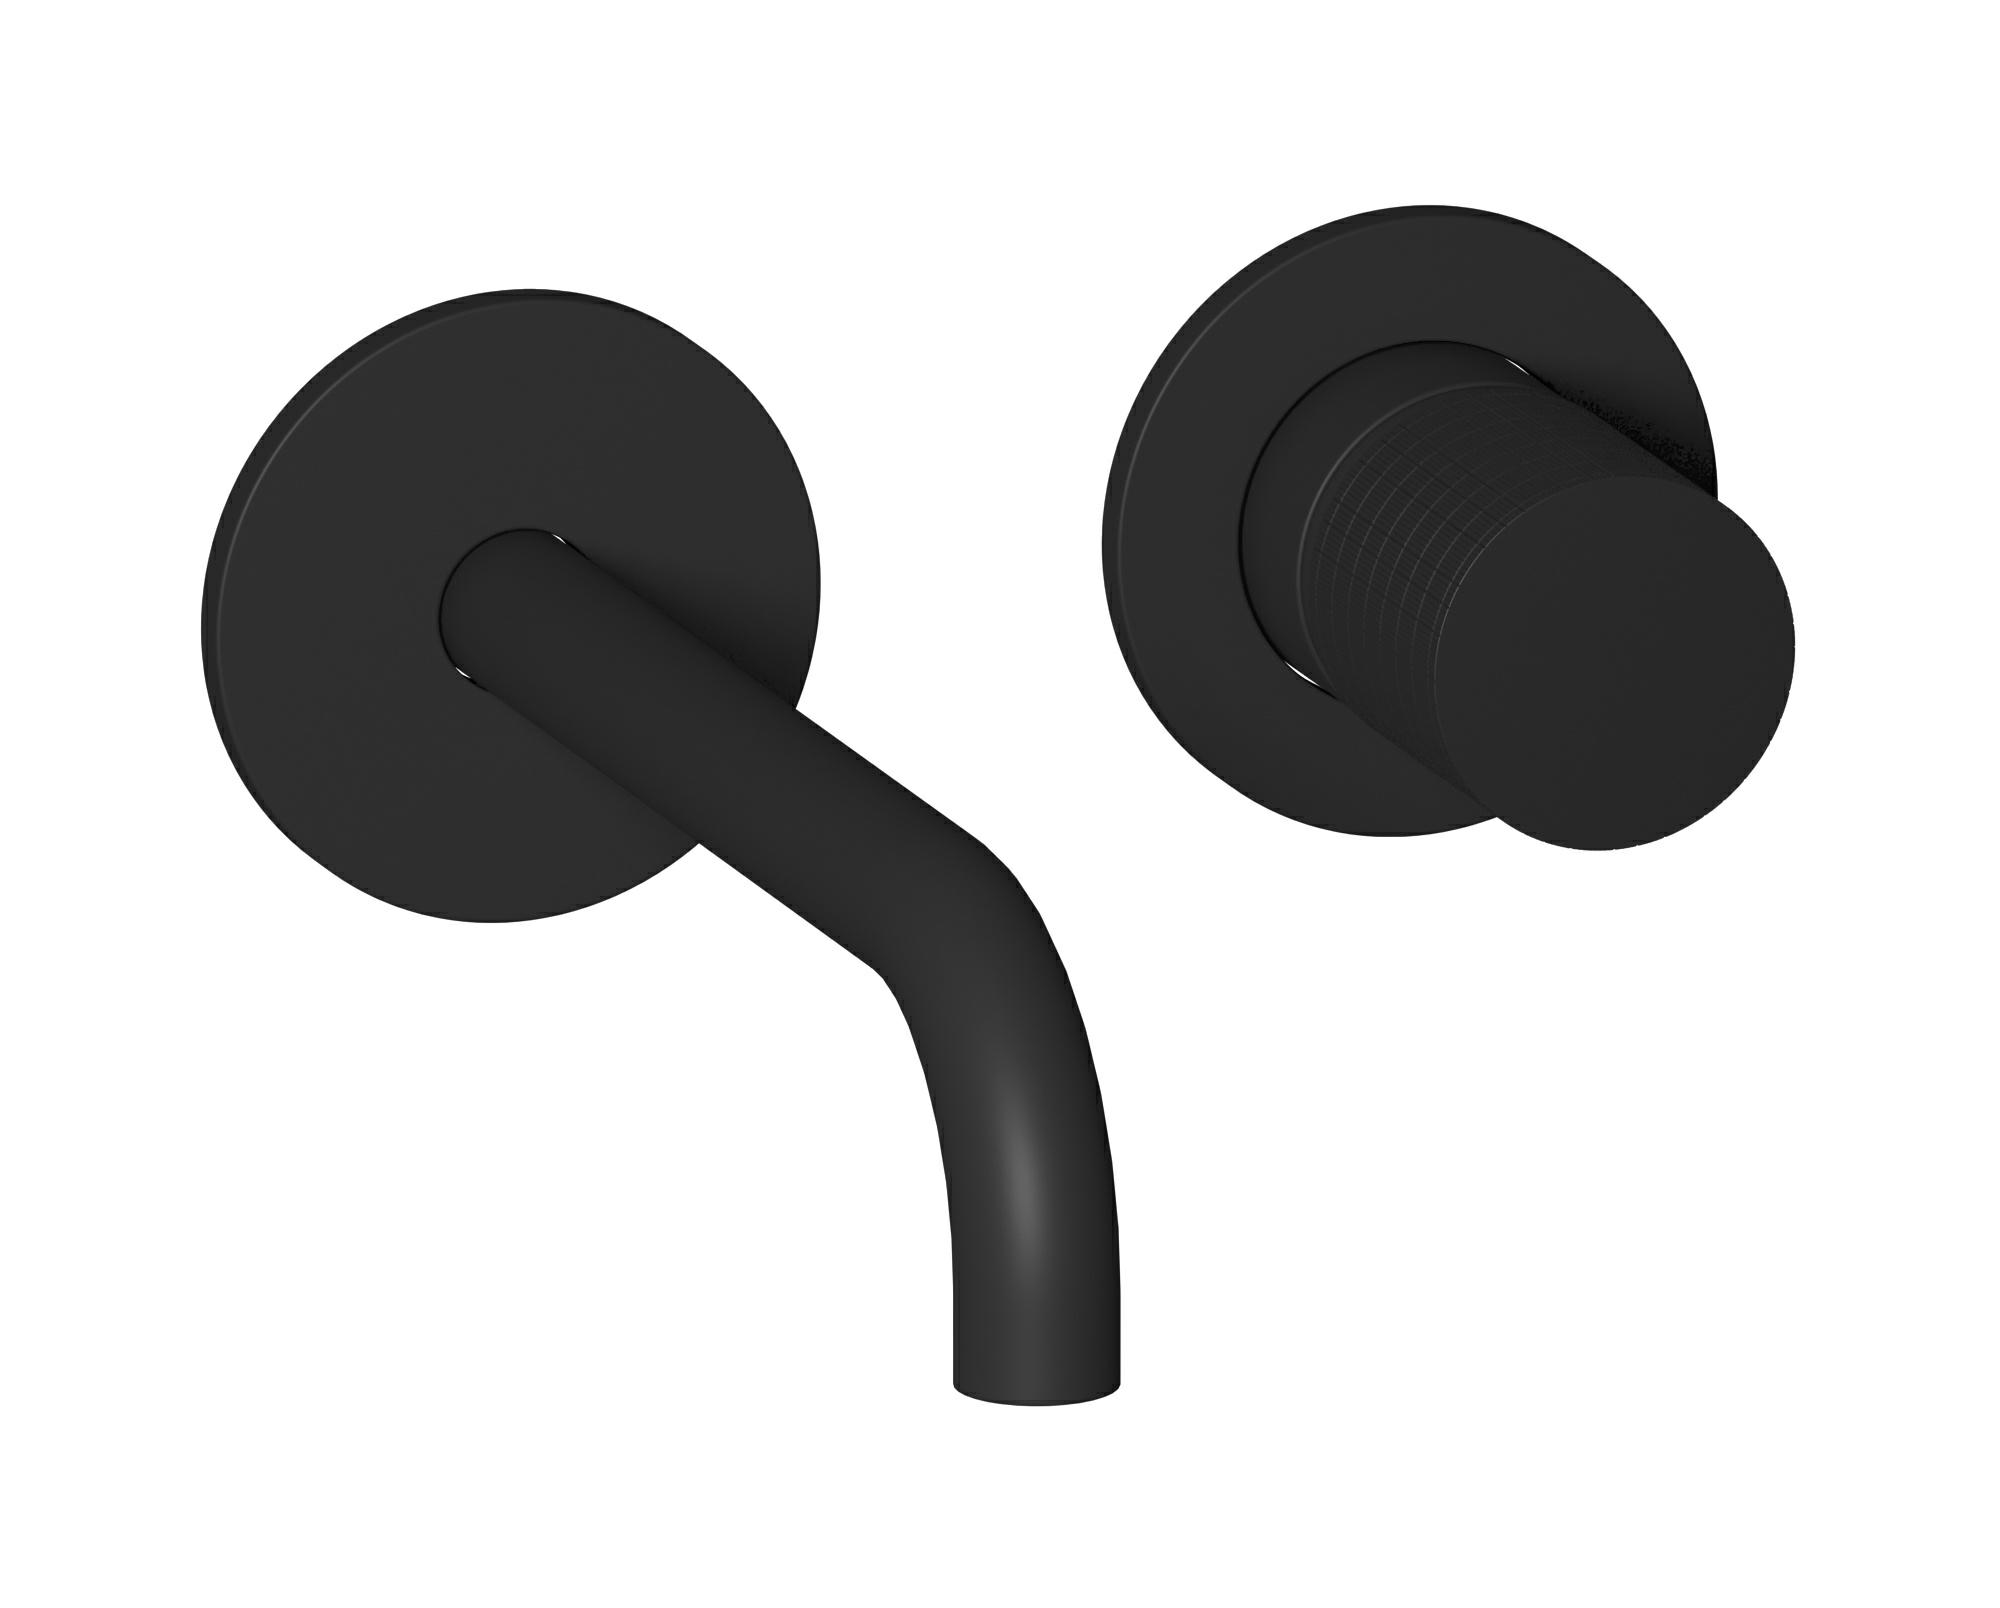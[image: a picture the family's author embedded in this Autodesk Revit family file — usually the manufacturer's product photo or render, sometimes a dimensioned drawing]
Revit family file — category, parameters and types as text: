
# Revit family: GA406
name_source: partatom
category: Apparecchi idraulici
units: mm (PartAtom-declared; Revit-internal decimal feet)

## family parameters
Basato su piano di lavoro = No
Condiviso = No
Mantieni orientamento annotazione = No
Numero OmniClass = 23.45.55.17
Punto di calcolo locali = No
Quota connettore circolare = Usa diametro
Sempre verticale = Sì
Taglio con vuoti quando caricato = No
Tipo di parte = Normale
Titolo OmniClass = Mixing Faucets

## types (12) — shared parameters
Cold water inlet = 10 mm  [stored 0.0328084 ft]
Commenti sul tipo = Wall mounted washbasin mixer complete with drain with rings
Connessione CW = No
Connessione HW = No
Connessione di scarico = No
Connessione di ventilazione = No
Descrizione = Wall mounted washbasin mixer complete with drain with rings
Hot water inlet = 10 mm  [stored 0.0328084 ft]
Produttore = IB Rubinetterie S.p.A.
URL = https://www.weareib.it
zero-valued in all types: Prospetto di default

## per-type parameters (varying)
| type | Finishes surface | Immagine tipo | Modello |
| Chrome | IB_Chrome | GA406CC.jpg | GA406CC |
| Black Chrome | IB_Black chrome | GA406CF.jpg | GA406CF |
| Brushed Black Chrome | IB_Brushed black chrome | GA406CS.jpg | GA406CS |
| Pale Gold | IB_Pale gold | GA406II.jpg | GA406II |
| Brushed Pale Gold | IB_brushed pale gold | GA406IS.jpg | GA406IS |
| Modern Bronze | IB_Modern bronze | GA406MB.jpg | GA406MB |
| Matt Black | IB_matt black | GA406NP.jpg | GA406NP |
| Gold | IB_gold | GA406OO.jpg | GA406OO |
| Brushed Gold | IB_brushed gold | GA406OS.jpg | GA406OS |
| Rose Gold | IB_Rose gold | GA406RS.jpg | GA406RS |
| Brushed Rose Gold | IB_Brushed rose gold | GA406SR.jpg | GA406SR |
| Brushed Nickel | IB_Brushed nickel | GA406SS.jpg | GA406SS |

note: [stored X ft] marks values corroborated as IEEE doubles in the binary element streams (Revit-internal decimal feet)
